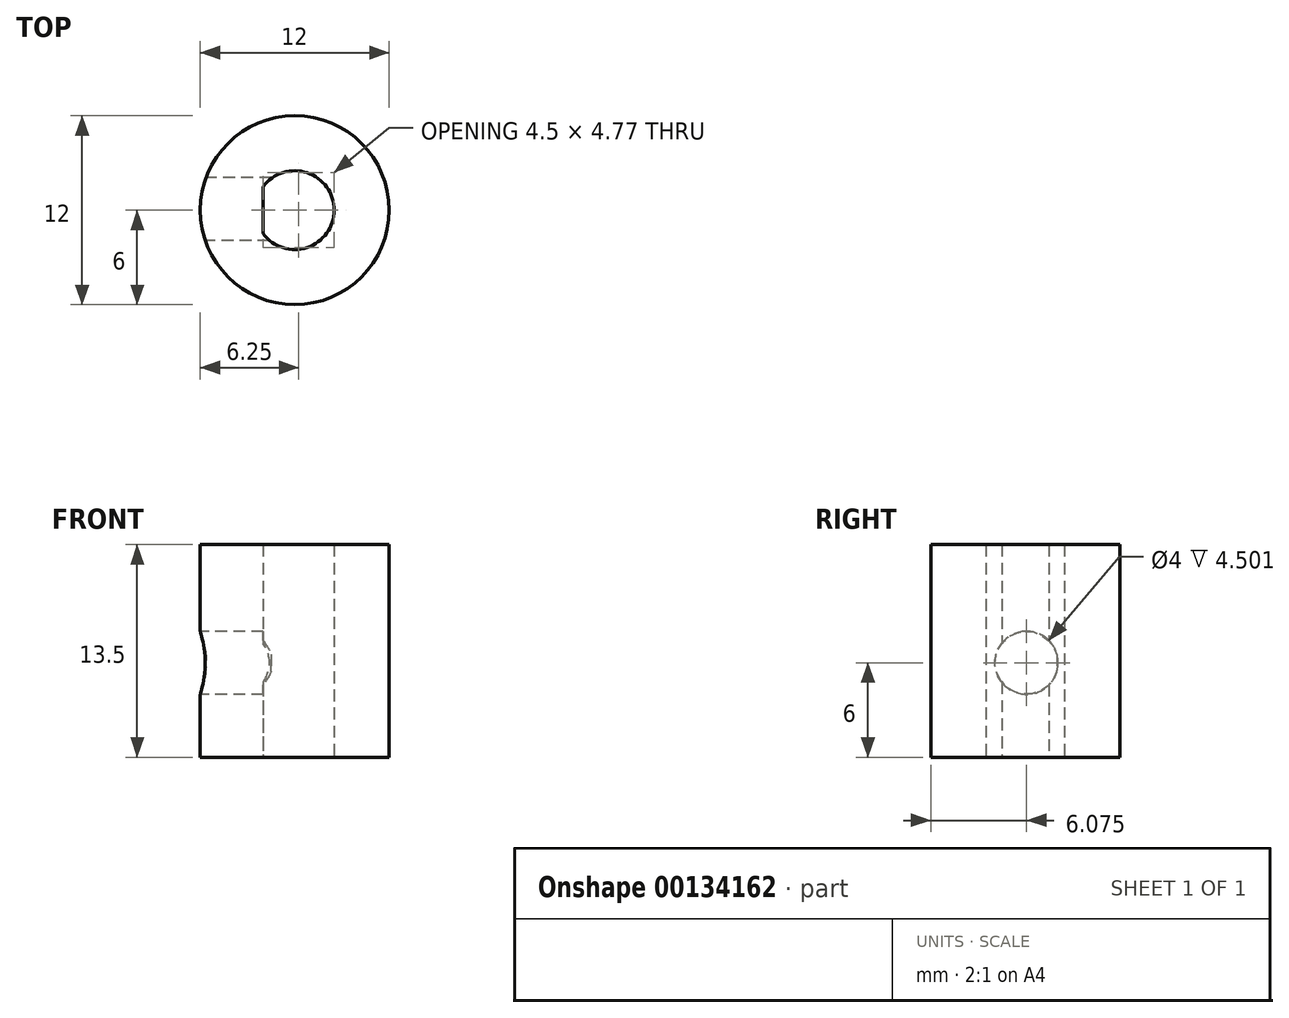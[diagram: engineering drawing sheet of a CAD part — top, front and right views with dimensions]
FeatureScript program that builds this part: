
annotation { "Feature Type Name" : "Feature", "Feature Type Description" : "" }
export const myFeature = defineFeature(function(context is Context, id is Id, definition is map)
    precondition{}
    {
        {
            var Q0;
            Q0=qCreatedBy(makeId("Top.planeOp"),FACE);
            var sketch = newSketch(context, id + "F0", { "sketchPlane" : qUnion([Q0])});
            skCircle(sketch, "E0", {"center": v(0, 0) * mm, "radius": 6 * mm});
            skArc(sketch, "E1", {"start": v(-2, -1.5) * mm, "mid": v(2.5, 0) * mm, "end": v(-2, 1.5) * mm});
            skLineSegment(sketch, "E2", {"start": v(-2, 1.5) * mm, "end": v(-2, -1.5) * mm});
            skSolve(sketch);
        }
        {
            var Q0;
            Q0=makeQuery(id+"F0.imprint","IMPRINT",FACE,{"disambiguationData":[TD([[makeQuery(id+"F0.imprint","IMPRINT",EDGE,{"derivedFrom":sQuery(id+"F0.wireOp",EDGE,"E0")}),1.0]])]});
            extrude(context, id + "F1", {"entities" : qUnion([Q0]), "depth" : 13.5 * mm});
        }
        {
            var Q0;
            Q0=makeQuery(id+"F1.opExtrude","SWEPT_FACE",FACE,{"disambiguationData":[OSD([sQuery(id+"F0.wireOp",EDGE,"E2")])]});
            cPlane(context, id + "F2", {"entities" : qUnion([Q0]), "cplaneType" : CPlaneType.OFFSET, "offset" : 4.5 * mm, "oppositeDirection" : true, "width" : 150 * mm, "height" : 150 * mm});
        }
        {
            var Q0;
            Q0=qCreatedBy(id+"F2.planeOp",FACE);
            var sketch = newSketch(context, id + "F3", { "sketchPlane" : qUnion([Q0])});
            skCircle(sketch, "E3", {"center": v(0.08, 6) * mm, "radius": 2 * mm});
            skSolve(sketch);
        }
        {
            var Q0;
            Q0=makeQuery(id+"F3.imprint","IMPRINT",FACE,{"disambiguationData":[TD([[makeQuery(id+"F3.imprint","IMPRINT",EDGE,{"derivedFrom":sQuery(id+"F3.wireOp",EDGE,"E3")}),1.0]])]});
            extrude(context, id + "F4", {"entities" : qUnion([Q0]), "operationType" : NewBodyOperationType.REMOVE, "depth" : 5 * mm});
        }
        {
            var Q0;
            Q0=makeQuery(id+"F1.opExtrude","CAP_FACE",FACE,{"disambiguationData":[OSD([sQuery(id+"F0.wireOp",EDGE,"E0"),sQuery(id+"F0.wireOp",EDGE,"E1"),sQuery(id+"F0.wireOp",EDGE,"E2")])],"isStart":false});
            var sketch = newSketch(context, id + "F5", { "sketchPlane" : qUnion([Q0])});
            skCircle(sketch, "E4", {"center": v(0, 0) * mm, "radius": 4.75 * mm});
            skSolve(sketch);
        }
        {
            var Q0;
            Q0=makeQuery(id+"F5.imprint","IMPRINT",FACE,{"disambiguationData":[TD([[makeQuery(id+"F5.imprint","IMPRINT",EDGE,{"derivedFrom":sQuery(id+"F5.wireOp",EDGE,"E4")}),-1.0]])]});
            cPlane(context, id + "F6", {"entities" : qUnion([Q0]), "cplaneType" : CPlaneType.OFFSET, "offset" : 3.5 * mm, "oppositeDirection" : true, "width" : 150 * mm, "height" : 150 * mm});
        }
    });
